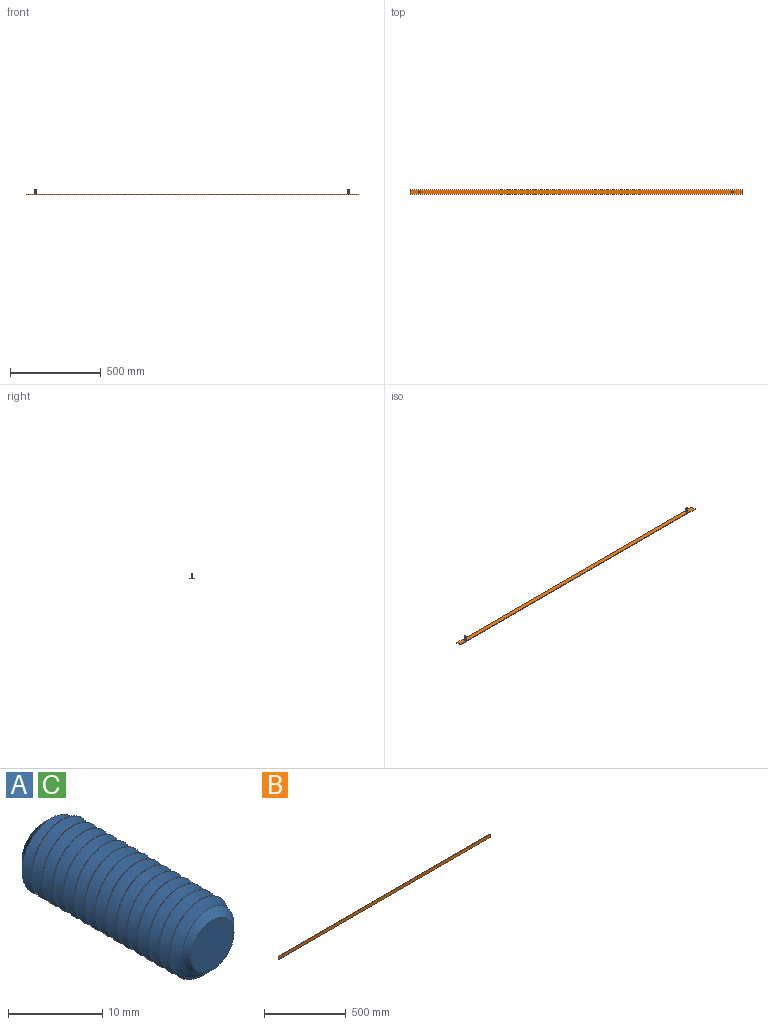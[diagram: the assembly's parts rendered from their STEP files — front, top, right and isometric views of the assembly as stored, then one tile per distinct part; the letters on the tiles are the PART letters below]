
ASSEMBLY  parts=3 mates=2
PART A: 8 faces, bbox 9.5x26.3x11 mm
  f0: cylinder r=4.76mm len=22.35mm, axis (0,1,0), area 57mm2, adj f3,f4,f6,f7
  f1: plane 6.48x6.48mm, normal (0,-1,0), area 32.9mm2, adj f3
  f2: plane 6.48x6.48mm, normal (0,1,0), area 32.9mm2, adj f4
  f3: cone r=3.24mm half-angle=45deg, axis (0,1,0), area 30mm2, adj f0,f1,f6,f7
  f4: cone r=4.76mm half-angle=45deg, axis (0,-1,0), area 36mm2, adj f0,f2,f5,f7
  f5: plane 0.97x0.95mm, normal (0.72,0,-0.7), area 0.3mm2, adj f4,f6,f7
  f6: bspline ~25.57x11mm, area 573.6mm2, adj f0,f3,f5,f7
  f7: bspline ~25.57x11mm, area 575.5mm2, adj f0,f3,f4,f5,f6
PART B: 6 faces, bbox 1828.8x3.2x25.4 mm
  f0: plane 1828.8x3.18mm, normal (0,0,-1), area 5806.4mm2, adj f1,f3,f4,f5
  f1: plane 25.4x3.18mm, normal (1,0,0), area 80.6mm2, adj f0,f2,f4,f5
  f2: plane 1828.8x3.18mm, normal (0,0,1), area 5806.4mm2, adj f1,f3,f4,f5
  f3: plane 25.4x3.18mm, normal (-1,0,0), area 80.6mm2, adj f0,f2,f4,f5
  f4: plane 1828.8x25.4mm, normal (0,-1,0), area 46451.5mm2, adj f0,f1,f2,f3
  f5: plane 1828.8x25.4mm, normal (0,1,0), area 46451.5mm2, adj f0,f1,f2,f3
PART C: same geometry as A
PLACE A rot(axis=(1,0,0),90deg) t=(-804.79,-12.5,127.98)mm
PLACE B rot(axis=(1,0,0),90deg) t=(973.21,0.2,102.58)mm
PLACE C rot(axis=(1,0,0),90deg) t=(922.41,-12.5,127.98)mm
MATE fastened A.f0 <-> B.f5  axis (0,0,-1) through (-804.79,-12.5,102.58)mm
MATE fastened C.f0 <-> B.f5  axis (0,0,-1) through (922.41,-12.5,102.58)mm
